# Revit family: Storage-Freestanding-Teknion-BSLFS_Lateral_File-R2019
name_source: partatom
category: Furniture
units: mm (PartAtom-declared; Revit-internal decimal feet)

## family parameters
Always vertical = Yes
Cut with Voids When Loaded = No
OmniClass Number = 23.40.70.14.64.21
OmniClass Title = Systems Furniture
Room Calculation Point = No
Shared = Yes
Work Plane-Based = No

## types (3) — shared parameters
Assembly Code = E2020200
Manufacturer = Teknion
Manufacturer Fax = 416.661.4586
Part Number = BSLFS
Product Documentation Link = http://www.teknion.com
Product Line = Expansion Casegoods
Product Page URL = https://www.teknion.com
Sustainability Data = http://www.teknion.com
Two Drawers Hole Depth = 2.701 "
URL = http://www.teknion.com
Unit Weight URL = http://www.teknion.com
Warranty = http://www.teknion.com

## per-type parameters (varying)
| type | Description | Four Drawer Hole Depth | Model | Second Drawer from Top | Three Drawers Hole Depth |
| Two Drawers | Lateral File, Pulls, Two Drawers, 28" Height | 0.5 " | BSLFSP____28 | No | 0.5 " |
| Three Drawers | Lateral File, Pulls, Three Drawers, 18" Depth, 40" Height | 0.5 " | BSLFSP18__40 | Yes | 2.701 " |
| Four Drawers | Lateral File, Pulls, Four Drawers, 18" Depth, 53" Height | 2.701 " | BSLFSP18__53 | Yes | 2.701 " |

type visibility flags: 3 boolean params named "<type name>" — each type sets only its own to Yes (folded from table)

## geometry (parser evidence)
native form markers: Blend x6, Sweep x2
no freeform markers — native parametric forms only
